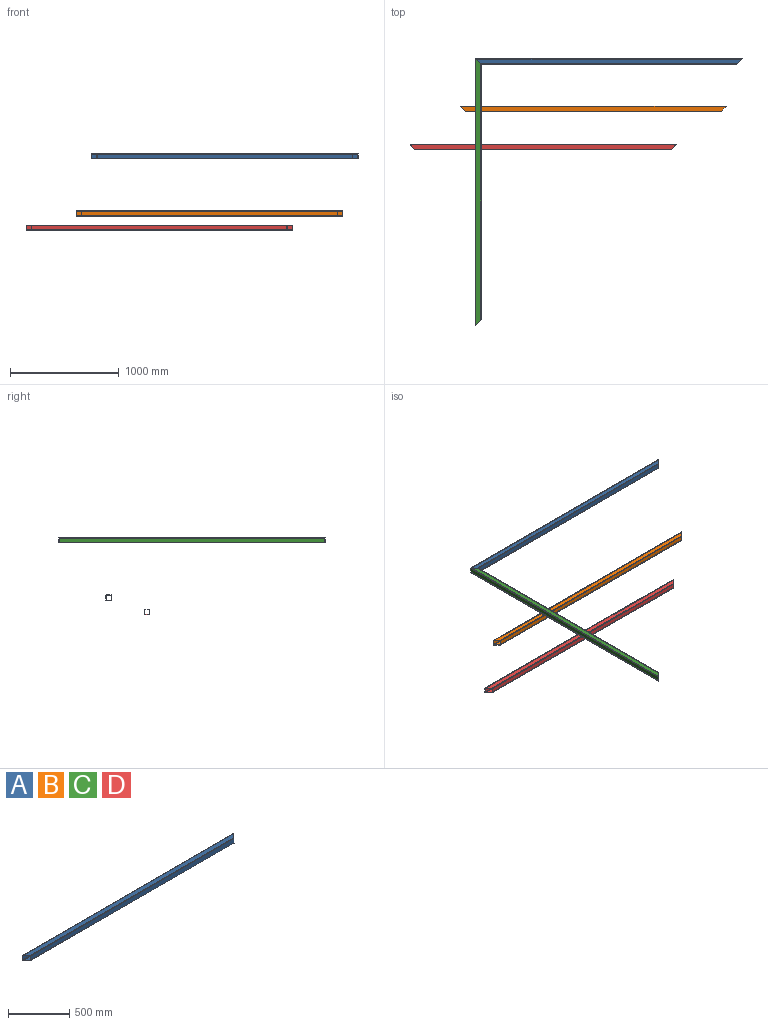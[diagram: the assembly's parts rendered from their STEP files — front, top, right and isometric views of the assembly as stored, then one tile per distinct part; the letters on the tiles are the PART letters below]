
ASSEMBLY  parts=4 mates=1
PART A: 18 faces, bbox 2447.9x50.8x50.8 mm
  f0: plane 2441.58x44.45mm, normal (0,0,1), area 106552.2mm2, adj f1,f13,f16,f17
  f1: cylinder r=3.17mm len=2352.68mm, axis (-1,0,0), area 11713.3mm2, adj f0,f14,f16,f17
  f2: cylinder r=3.17mm len=2352.68mm, axis (-1,0,0), area 11713.3mm2, adj f3,f14,f16,f17
  f3: plane 2441.58x44.45mm, normal (0,0,-1), area 106552.2mm2, adj f2,f4,f16,f17
  f4: cylinder r=3.17mm len=2447.93mm, axis (-1,0,0), area 12197mm2, adj f3,f15,f16,f17
  f5: cylinder r=3.17mm len=2359.03mm, axis (-1,0,0), area 11745mm2, adj f6,f12,f16,f17
  f6: plane 2435.23x38.1mm, normal (0,0,-1), area 91330.5mm2, adj f5,f7,f16,f17
  f7: cylinder r=3.17mm len=2441.58mm, axis (-1,0,0), area 12165.3mm2, adj f6,f8,f16,f17
  f8: plane 2441.58x38.1mm, normal (0,-1,0), area 93024mm2, adj f7,f9,f16,f17
  f9: cylinder r=3.17mm len=2441.58mm, axis (-1,0,0), area 12165.3mm2, adj f8,f10,f16,f17
  f10: plane 2435.23x38.1mm, normal (0,0,1), area 91330.5mm2, adj f9,f11,f16,f17
  f11: cylinder r=3.17mm len=2359.03mm, axis (-1,0,0), area 11745mm2, adj f10,f12,f16,f17
  f12: plane 2352.68x38.1mm, normal (0,1,0), area 89636.9mm2, adj f5,f11,f16,f17
  f13: cylinder r=3.17mm len=2447.93mm, axis (-1,0,0), area 12197mm2, adj f0,f15,f16,f17
  f14: plane 2346.33x44.45mm, normal (0,-1,0), area 104294.1mm2, adj f1,f2,f16,f17
  f15: plane 2447.93x44.45mm, normal (0,1,0), area 108810.3mm2, adj f4,f13,f16,f17
  f16: plane 50.8x50.8mm, normal (-0.71,-0.71,0), area 855.4mm2, adj f0,f1,f2,f3,f4,f5,f6,f7
  f17: plane 50.8x50.8mm, normal (0.71,-0.71,0), area 855.4mm2, adj f0,f1,f2,f3,f4,f5,f6,f7
PART B: same geometry as A
PART C: same geometry as A
PART D: same geometry as A
PLACE A t=(-17.14,710.89,21.2)mm
PLACE B t=(-158.86,277.45,-506.23)mm
PLACE C rot(axis=(0,0,1),90deg) t=(8.26,-1711.63,21.2)mm
PLACE D t=(-618.58,-74.43,-635.92)mm
MATE fastened C.f17 <-> A.f16  axis (0.71,0.71,0) through (-17.14,736.29,21.2)mm
